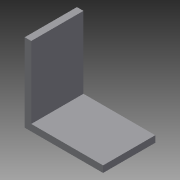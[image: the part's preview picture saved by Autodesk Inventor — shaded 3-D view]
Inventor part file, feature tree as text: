
AUTODESK INVENTOR PART (.ipt)
format: ipt  version: 2015 (Build 190159000, 159)  size: 79,872 bytes
history: native  units: in
note: dims shown in document units (in); Inventor stores cm internally (conversion verified against a paired STEP export)
features: extrude x2, sketch x2
ambient origin geometry x8: Origin, YZ Plane, XZ Plane, XY Plane, X Axis, Y Axis, Z Axis, Center Point
bodies: Solid1 (feature_tree)
feature tree (4):
  extrude  "Extrusion1"  Depth=0.125in
  extrude  "Extrusion2"  Depth=0.125in
  sketch  "Sketch1"  dims[d0=1.5in d1=0.125in]
  sketch  "Sketch2"  dims[d2=1.0in d3=0.0in d4=0.125in d5=1.5in d6=1.0in d7=0.0in]
